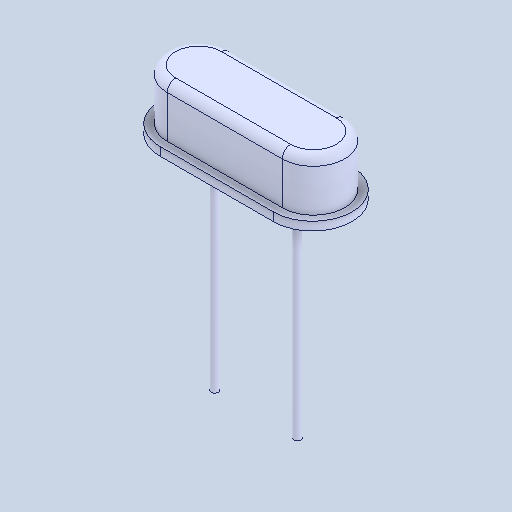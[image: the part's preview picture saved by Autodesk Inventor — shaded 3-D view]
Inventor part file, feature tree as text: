
AUTODESK INVENTOR PART (.ipt)
format: ipt  version: 2024 (Build 280153000, 153)  size: 128,512 bytes
history: native  units: mm
features: other x2, fillet x1
ambient origin geometry x8: Origin, YZ Plane, XZ Plane, XY Plane, X Axis, Y Axis, Z Axis, Center Point
bodies: Solide1 (feature_tree), Solide2 (feature_tree), Solide3 (feature_tree)
feature tree (3):
  fillet  "Fillet1"  [1 undecoded]
  other  "Boss-Extrude3[1]"
  other  "Boss-Extrude3[2]"
note: 1 required parameter value undecoded (feature->parameter linkage not recoverable at this tier; creation-order binding heuristic only, values carry confidence <= 0.55)
